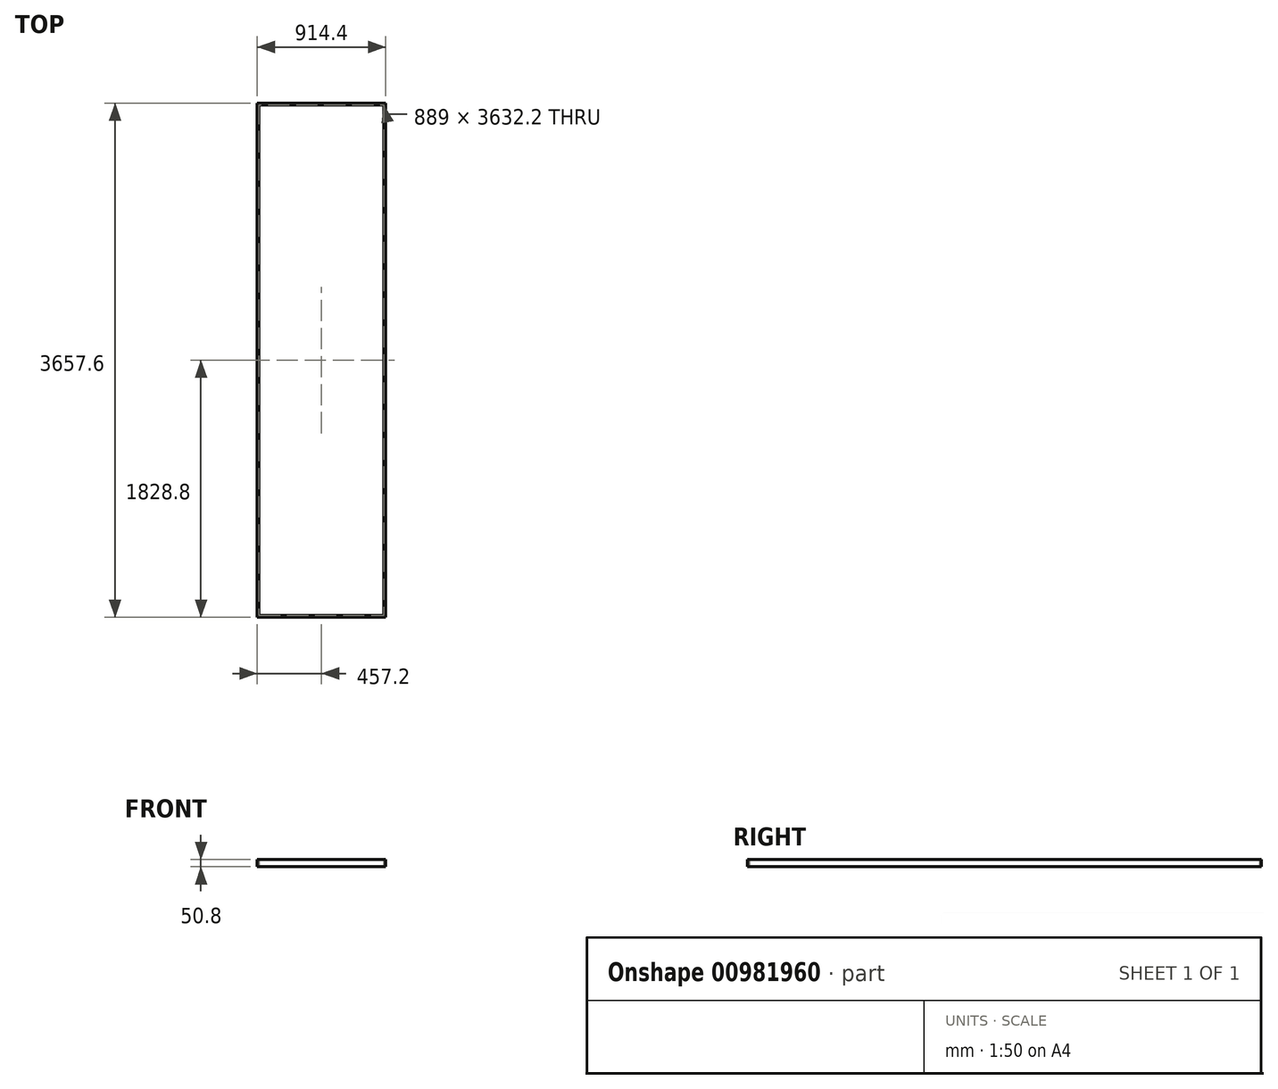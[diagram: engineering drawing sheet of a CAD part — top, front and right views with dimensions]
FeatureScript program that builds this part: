
annotation { "Feature Type Name" : "Feature", "Feature Type Description" : "" }
export const myFeature = defineFeature(function(context is Context, id is Id, definition is map)
    precondition{}
    {
        {
            var Q0;
            Q0=qCreatedBy(makeId("Top.planeOp"),FACE);
            var sketch = newSketch(context, id + "F0", { "sketchPlane" : qUnion([Q0])});
            skLineSegment(sketch, "E0.bottom", {"start": v(457.2, 1828.8) * mm, "end": v(-457.2, 1828.8) * mm});
            skLineSegment(sketch, "E0.top", {"start": v(457.2, -1828.8) * mm, "end": v(-457.2, -1828.8) * mm});
            skLineSegment(sketch, "E0.left", {"start": v(457.2, 1828.8) * mm, "end": v(457.2, -1828.8) * mm});
            skLineSegment(sketch, "E0.right", {"start": v(-457.2, 1828.8) * mm, "end": v(-457.2, -1828.8) * mm});
            skPoint(sketch, "E0.middle", {"position": v(0, 0) * mm});
            skLineSegment(sketch, "E1.bottom", {"start": v(-444.5, 1816.1) * mm, "end": v(444.5, 1816.1) * mm});
            skLineSegment(sketch, "E1.top", {"start": v(-444.5, -1816.1) * mm, "end": v(444.5, -1816.1) * mm});
            skLineSegment(sketch, "E1.left", {"start": v(-444.5, 1816.1) * mm, "end": v(-444.5, -1816.1) * mm});
            skLineSegment(sketch, "E1.right", {"start": v(444.5, 1816.1) * mm, "end": v(444.5, -1816.1) * mm});
            skSolve(sketch);
        }
        {
            var Q0;
            Q0=makeQuery(id+"F0.imprint","IMPRINT",FACE,{"disambiguationData":[TD([[makeQuery(id+"F0.imprint","IMPRINT",EDGE,{"derivedFrom":sQuery(id+"F0.wireOp",EDGE,"E0.bottom")}),1.0]])]});
            extrude(context, id + "F1", {"entities" : qUnion([Q0]), "depth" : 50.8 * mm, "offsetDistance" : 25.4 * mm});
        }
    });
